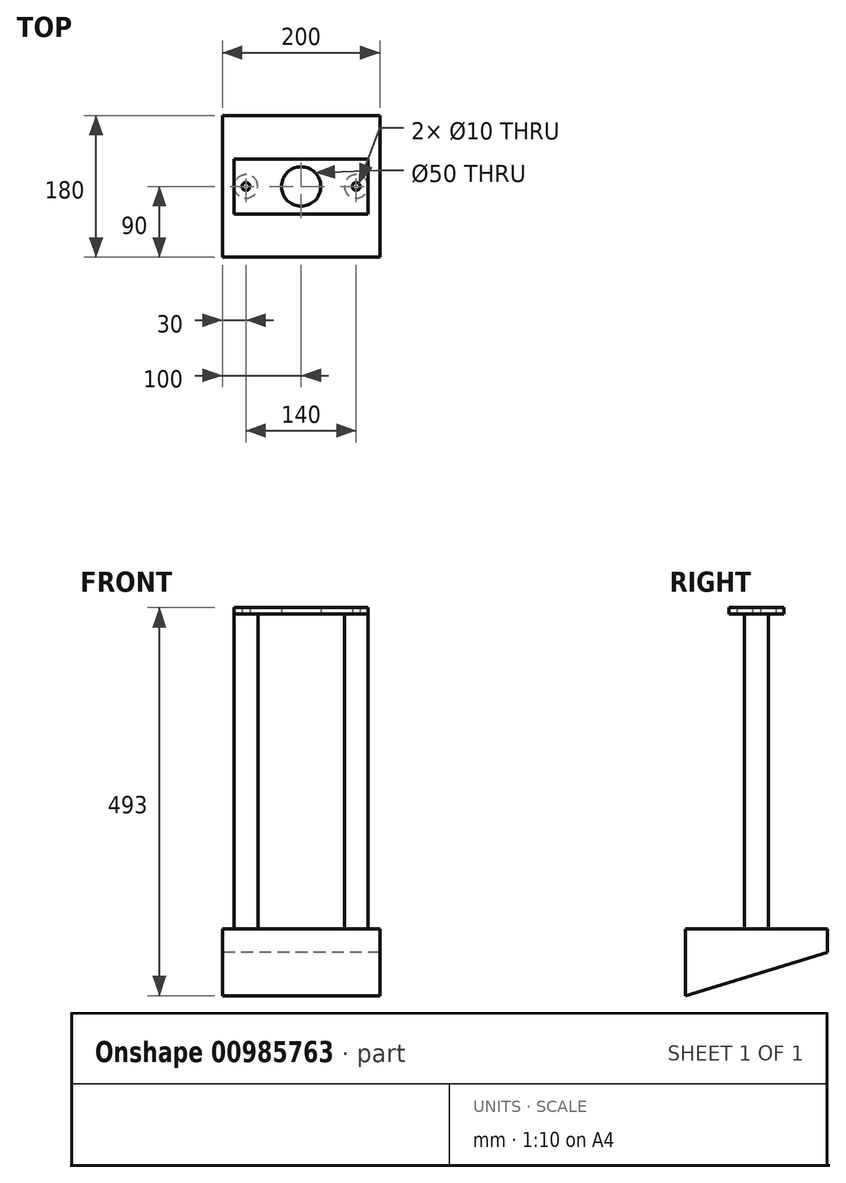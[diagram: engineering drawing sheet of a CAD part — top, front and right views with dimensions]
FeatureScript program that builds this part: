
annotation { "Feature Type Name" : "Feature", "Feature Type Description" : "" }
export const myFeature = defineFeature(function(context is Context, id is Id, definition is map)
    precondition{}
    {
        {
            var Q0;
            Q0=qCreatedBy(makeId("Top.planeOp"),FACE);
            var sketch = newSketch(context, id + "F0", { "sketchPlane" : qUnion([Q0])});
            skLineSegment(sketch, "E0.bottom", {"start": v(85, 35) * mm, "end": v(-85, 35) * mm});
            skLineSegment(sketch, "E0.top", {"start": v(85, -35) * mm, "end": v(-85, -35) * mm});
            skLineSegment(sketch, "E0.left", {"start": v(85, 35) * mm, "end": v(85, -35) * mm});
            skLineSegment(sketch, "E0.right", {"start": v(-85, 35) * mm, "end": v(-85, -35) * mm});
            skPoint(sketch, "E0.middle", {"position": v(0, 0) * mm});
            skCircle(sketch, "E1", {"center": v(-70, 0) * mm, "radius": 5 * mm});
            skCircle(sketch, "E2", {"center": v(0, 0) * mm, "radius": 25 * mm});
            skCircle(sketch, "E3.MirrorC", {"center": v(70, 0) * mm, "radius": 5 * mm});
            skSolve(sketch);
        }
        {
            var Q0;
            Q0=makeQuery(id+"F0.imprint","IMPRINT",FACE,{"disambiguationData":[TD([[makeQuery(id+"F0.imprint","IMPRINT",EDGE,{"derivedFrom":sQuery(id+"F0.wireOp",EDGE,"E0.bottom")}),1.0]])]});
            extrude(context, id + "F1", {"entities" : qUnion([Q0]), "depth" : 8 * mm, "offsetDistance" : 25 * mm});
        }
        {
            var Q0;
            Q0=qCreatedBy(makeId("Top.planeOp"),FACE);
            var sketch = newSketch(context, id + "F2", { "sketchPlane" : qUnion([Q0])});
            skCircle(sketch, "E4", {"center": v(-70, 0) * mm, "radius": 15 * mm});
            skCircle(sketch, "E5", {"center": v(70, 0) * mm, "radius": 15 * mm});
            skSolve(sketch);
        }
        {
            var Q0;
            Q0 = qSketchRegion(id + "F2", true);
            extrude(context, id + "F3", {"entities" : qUnion([Q0]), "oppositeDirection" : true, "depth" : 400 * mm, "offsetDistance" : 25 * mm});
        }
        {
            var Q0;
            Q0=qCreatedBy(makeId("Right.planeOp"),FACE);
            var sketch = newSketch(context, id + "F4", { "sketchPlane" : qUnion([Q0])});
            skLineSegment(sketch, "E6", {"start": v(90, -400) * mm, "end": v(-90, -400) * mm});
            skLineSegment(sketch, "E7", {"start": v(-90, -400) * mm, "end": v(-90, -485) * mm});
            skLineSegment(sketch, "E8", {"start": v(-90, -485) * mm, "end": v(90, -430) * mm});
            skLineSegment(sketch, "E9", {"start": v(90, -430) * mm, "end": v(90, -400) * mm});
            skSolve(sketch);
        }
        {
            var Q0;
            Q0=makeQuery(id+"F4.imprint","IMPRINT",FACE,{"disambiguationData":[TD([[makeQuery(id+"F4.imprint","IMPRINT",EDGE,{"derivedFrom":sQuery(id+"F4.wireOp",EDGE,"E6")}),1.0]])]});
            extrude(context, id + "F5", {"entities" : qUnion([Q0]), "endBound" : BoundingType.SYMMETRIC, "depth" : 200 * mm, "offsetDistance" : 25 * mm});
        }
    });
